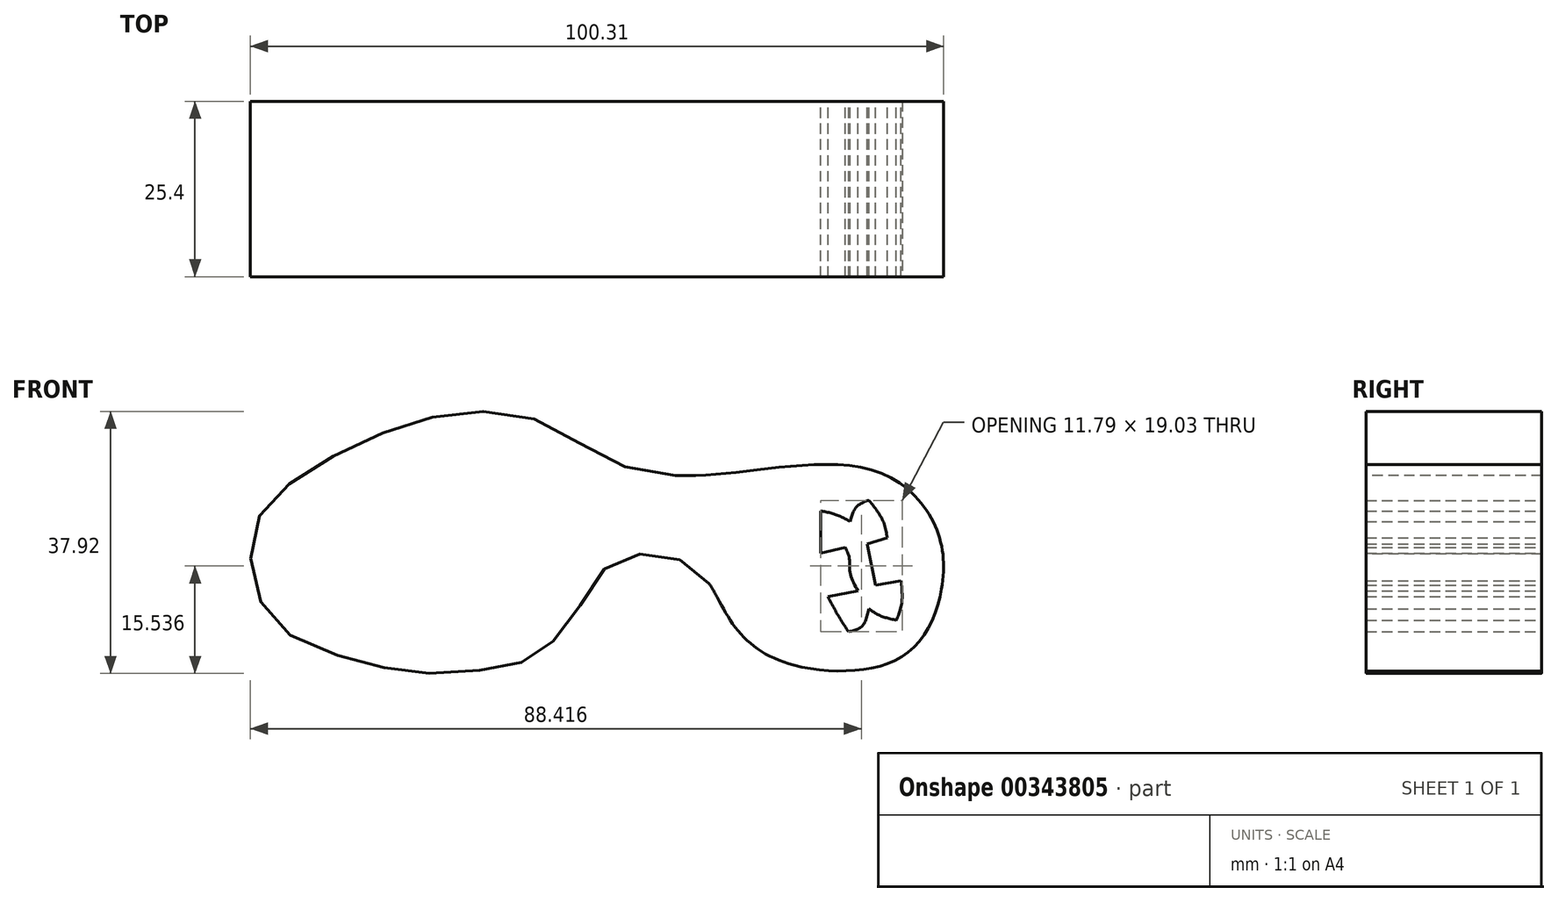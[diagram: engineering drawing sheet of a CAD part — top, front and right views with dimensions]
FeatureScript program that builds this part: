
annotation { "Feature Type Name" : "Feature", "Feature Type Description" : "" }
export const myFeature = defineFeature(function(context is Context, id is Id, definition is map)
    precondition{}
    {
        {
            var Q0;
            Q0=qCreatedBy(makeId("Front.planeOp"),FACE);
            var sketch = newSketch(context, id + "F0", { "sketchPlane" : qUnion([Q0])});
            skFitSpline(sketch, "E0", {"points": [v(29.88, -19.03) * mm, v(31.83, -18.2) * mm, v(32.8, -15.68) * mm], "startDerivative": vector(4.7, 1.08) * mm, "endDerivative": vector(1.23, 5.52) * mm});
            skFitSpline(sketch, "E1", {"points": [v(32.8, -15.68) * mm, v(34.34, -16.66) * mm, v(36.78, -17.35) * mm], "startDerivative": vector(3.08, -2.32) * mm, "endDerivative": vector(4.82, -1.06) * mm});
            skFitSpline(sketch, "E2", {"points": [v(36.78, -17.35) * mm, v(37.55, -14.98) * mm, v(37.48, -11.64) * mm], "startDerivative": vector(2.07, 4.86) * mm, "endDerivative": vector(-0.6, 6.53) * mm});
            skFitSpline(sketch, "E3", {"points": [v(37.48, -11.64) * mm, v(33.78, -12.26) * mm], "startDerivative": vector(-3.7, -0.63) * mm, "endDerivative": vector(-3.7, -0.63) * mm});
            skFitSpline(sketch, "E4", {"points": [v(33.78, -12.26) * mm, v(32.59, -6.34) * mm], "startDerivative": vector(-1.2, 5.93) * mm, "endDerivative": vector(-1.2, 5.93) * mm});
            skFitSpline(sketch, "E5", {"points": [v(32.59, -6.34) * mm, v(35.46, -5.43) * mm], "startDerivative": vector(2.87, 0.9) * mm, "endDerivative": vector(2.87, 0.9) * mm});
            skFitSpline(sketch, "E6", {"points": [v(35.46, -5.43) * mm, v(34.76, -2.78) * mm, v(32.8, 0) * mm], "startDerivative": vector(-0.95, 5.68) * mm, "endDerivative": vector(-4.3, 5.2) * mm});
            skFitSpline(sketch, "E7", {"points": [v(32.8, 0) * mm, v(31.06, -0.9) * mm, v(30.09, -3.06) * mm], "startDerivative": vector(-4.09, -1.35) * mm, "endDerivative": vector(-1.4, -4.71) * mm});
            skFitSpline(sketch, "E8", {"points": [v(30.09, -3.06) * mm, v(28.06, -2.08) * mm, v(25.83, -1.52) * mm], "startDerivative": vector(-3.98, 2.18) * mm, "endDerivative": vector(-4.53, 0.9) * mm});
            skFitSpline(sketch, "E9", {"points": [v(25.83, -1.52) * mm, v(25.83, -7.66) * mm], "startDerivative": vector(0, -6.14) * mm, "endDerivative": vector(0, -6.14) * mm});
            skFitSpline(sketch, "E10", {"points": [v(25.83, -7.66) * mm, v(29.39, -6.82) * mm], "startDerivative": vector(3.56, 0.84) * mm, "endDerivative": vector(3.56, 0.84) * mm});
            skFitSpline(sketch, "E11", {"points": [v(29.39, -6.82) * mm, v(29.96, -8.33) * mm, v(30.09, -10.5) * mm, v(31.2, -13.1) * mm], "startDerivative": vector(2.54, -4.95) * mm, "endDerivative": vector(3.8, -6.82) * mm});
            skFitSpline(sketch, "E12", {"points": [v(31.2, -13.1) * mm, v(26.88, -13.94) * mm], "startDerivative": vector(-4.32, -0.84) * mm, "endDerivative": vector(-4.32, -0.84) * mm});
            skFitSpline(sketch, "E13", {"points": [v(26.88, -13.94) * mm, v(28.28, -16.56) * mm, v(29.88, -19.03) * mm], "startDerivative": vector(2.68, -5.3) * mm, "endDerivative": vector(3.3, -4.88) * mm});
            skFitSpline(sketch, "E14", {"points": [v(-21.13, -24.27) * mm, v(-32.12, -25) * mm, v(-41.2, -23.24) * mm, v(-51.9, -18.85) * mm, v(-56.3, -11.52) * mm, v(-55.7, -2.88) * mm, v(-49.55, 3.42) * mm, v(-37.98, 9.57) * mm, v(-26.55, 12.65) * mm, v(-14.83, 11.48) * mm, v(-4.43, 5.62) * mm, v(7, 3.57) * mm, v(19.45, 4.74) * mm, v(34.39, 4) * mm, v(42.3, -3.46) * mm, v(43.32, -12.84) * mm, v(38.78, -21.78) * mm, v(28.97, -24.7) * mm, v(17.84, -22.22) * mm, v(12.12, -16.36) * mm, v(8.31, -10.35) * mm, v(2.16, -7.86) * mm, v(-4.58, -9.18) * mm, v(-9.41, -15.92) * mm, v(-14.98, -22.22) * mm, v(-21.13, -24.27) * mm]});
            skFitSpline(sketch, "E15", {"points": [v(-53.05, -10.15) * mm, v(-53.05, -8.77) * mm], "startDerivative": vector(0, 1.38) * mm, "endDerivative": vector(0, 1.38) * mm});
            skFitSpline(sketch, "E16", {"points": [v(-53.05, -8.77) * mm, v(-27.47, -10.5) * mm], "startDerivative": vector(25.57, -1.73) * mm, "endDerivative": vector(25.57, -1.73) * mm});
            skFitSpline(sketch, "E17", {"points": [v(-27.47, -10.5) * mm, v(-31.11, 5.7) * mm], "startDerivative": vector(-3.64, 16.2) * mm, "endDerivative": vector(-3.64, 16.2) * mm});
            skFitSpline(sketch, "E18", {"points": [v(-53.05, -10.15) * mm, v(-24.93, -12) * mm], "startDerivative": vector(28.12, -1.85) * mm, "endDerivative": vector(28.12, -1.85) * mm});
            skFitSpline(sketch, "E19", {"points": [v(-24.93, -12) * mm, v(-28.4, 3.03) * mm], "startDerivative": vector(-3.47, 15.04) * mm, "endDerivative": vector(-3.47, 15.04) * mm});
            skFitSpline(sketch, "E20", {"points": [v(-28.4, 3.03) * mm, v(10.89, -5.84) * mm], "startDerivative": vector(39.28, -8.88) * mm, "endDerivative": vector(39.28, -8.88) * mm});
            skFitSpline(sketch, "E21", {"points": [v(10.89, -5.84) * mm, v(9.67, -12) * mm], "startDerivative": vector(-1.22, -6.16) * mm, "endDerivative": vector(-1.22, -6.16) * mm});
            skFitSpline(sketch, "E22", {"points": [v(-31.11, 5.7) * mm, v(13.46, -4.83) * mm], "startDerivative": vector(44.58, -10.53) * mm, "endDerivative": vector(44.58, -10.53) * mm});
            skFitSpline(sketch, "E23", {"points": [v(13.46, -4.83) * mm, v(10.89, -14.1) * mm], "startDerivative": vector(-2.58, -9.27) * mm, "endDerivative": vector(-2.58, -9.27) * mm});
            skFitSpline(sketch, "E24", {"points": [v(21.9, -23.83) * mm, v(17.66, -13.97) * mm], "startDerivative": vector(-4.24, 9.85) * mm, "endDerivative": vector(-4.24, 9.85) * mm});
            skFitSpline(sketch, "E25", {"points": [v(17.66, -13.97) * mm, v(21.4, -5.9) * mm], "startDerivative": vector(3.73, 8.08) * mm, "endDerivative": vector(3.73, 8.08) * mm});
            skFitSpline(sketch, "E26", {"points": [v(21.4, -5.9) * mm, v(4.81, 3.6) * mm], "startDerivative": vector(-16.58, 9.62) * mm, "endDerivative": vector(-16.58, 9.62) * mm});
            skFitSpline(sketch, "E27", {"points": [v(43.32, -12.84) * mm, v(39.5, -10.98) * mm], "startDerivative": vector(-3.83, 1.86) * mm, "endDerivative": vector(-3.83, 1.86) * mm});
            skFitSpline(sketch, "E28", {"points": [v(39.5, -10.98) * mm, v(41.6, -6.69) * mm], "startDerivative": vector(2.1, 4.3) * mm, "endDerivative": vector(2.1, 4.3) * mm});
            skFitSpline(sketch, "E29", {"points": [v(41.76, -6.61) * mm, v(37.59, -4.13) * mm], "startDerivative": vector(-4.17, 2.49) * mm, "endDerivative": vector(-4.17, 2.49) * mm});
            skFitSpline(sketch, "E30", {"points": [v(37.59, -4.13) * mm, v(39.5, 0.61) * mm], "startDerivative": vector(1.91, 4.74) * mm, "endDerivative": vector(1.91, 4.74) * mm});
            skSolve(sketch);
        }
        {
            var Q0;
            Q0 = qSketchRegion(id + "F0", true);
            extrude(context, id + "F1", {"entities" : qUnion([Q0]), "depth" : 25.4 * mm});
        }
        {
            var Q0;
            Q0 = qSketchRegion(id + "F0", true);
            extrude(context, id + "F2", {"entities" : qUnion([Q0]), "operationType" : NewBodyOperationType.ADD, "depth" : 25.4 * mm});
        }
    });
